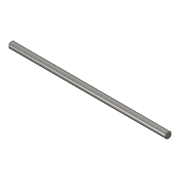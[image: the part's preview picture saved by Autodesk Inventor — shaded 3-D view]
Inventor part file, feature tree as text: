
AUTODESK INVENTOR PART (.ipt)
format: ipt  version: 2019.4 (Build 234330000, 330)  size: 78,848 bytes
history: native  units: in
note: dims shown in document units (in); Inventor stores cm internally (conversion verified against a paired STEP export)
features: extrude x1, chamfer x1, sketch x1
ambient origin geometry x8: Origin, YZ Plane, XZ Plane, XY Plane, X Axis, Y Axis, Z Axis, Center Point
bodies: Solid1 (feature_tree)
feature tree (3):
  extrude  "Extrusion1"  Depth=12.5in TaperAngle=0.0deg
  chamfer  "Chamfer1"  Distance=0.0625in Angle=45.0deg
  sketch  "Sketch1"  dims[d0=0.5in d1=12.5in d2=0.0in d3=0.0625in d4=0.125in d5=45.0deg]
